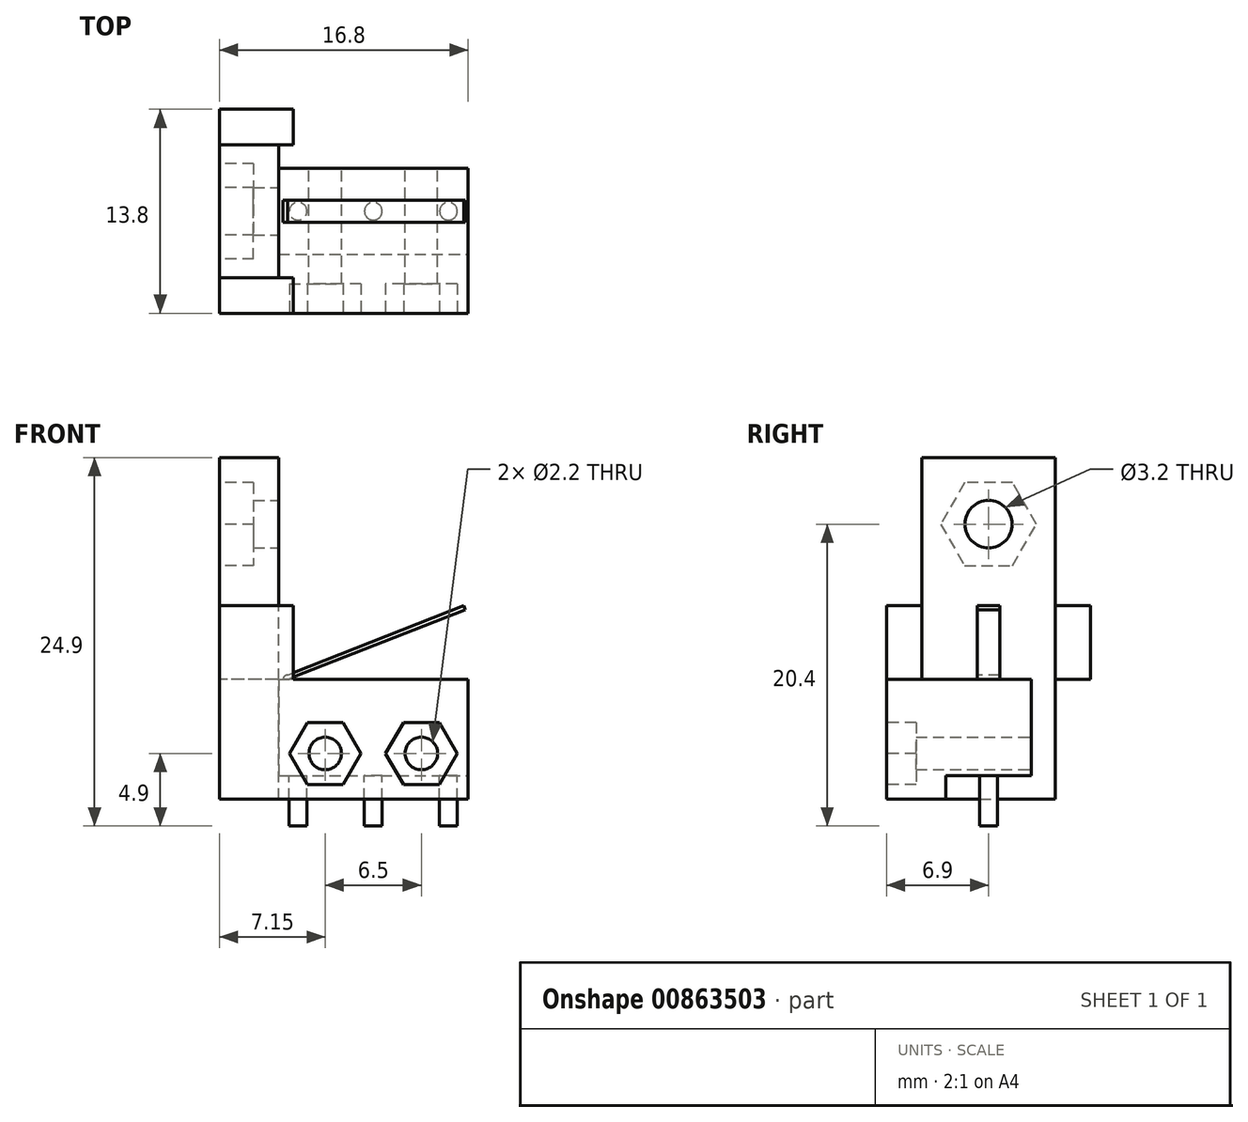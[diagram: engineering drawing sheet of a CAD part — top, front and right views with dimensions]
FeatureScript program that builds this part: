
annotation { "Feature Type Name" : "Feature", "Feature Type Description" : "" }
export const myFeature = defineFeature(function(context is Context, id is Id, definition is map)
    precondition{}
    {
        {
            var Q0;
            Q0=qCreatedBy(makeId("Front.planeOp"),FACE);
            var sketch = newSketch(context, id + "F0", { "sketchPlane" : qUnion([Q0])});
            skLineSegment(sketch, "E0.bottom", {"start": v(-6.4, 6.5) * mm, "end": v(6.4, 6.5) * mm});
            skLineSegment(sketch, "E0.top", {"start": v(-6.4, 0) * mm, "end": v(6.4, 0) * mm});
            skLineSegment(sketch, "E0.left", {"start": v(-6.4, 6.5) * mm, "end": v(-6.4, 0) * mm});
            skLineSegment(sketch, "E0.right", {"start": v(6.4, 6.5) * mm, "end": v(6.4, 0) * mm});
            skCircle(sketch, "E1", {"center": v(3.25, 1.5) * mm, "radius": 1.1 * mm});
            skCircle(sketch, "E2", {"center": v(-3.25, 1.5) * mm, "radius": 1.1 * mm});
            skLineSegment(sketch, "E3", {"start": v(0, 0.48) * mm, "end": v(0, 13.87) * mm, "construction": true});
            skSolve(sketch);
        }
        {
            var Q0;
            Q0=qSketchRegion(id+"F0",true);
            extrude(context, id + "F1", {"entities" : qUnion([Q0]), "depth" : 5.8 * mm});
        }
        {
            var Q0;
            Q0=makeQuery(id+"F1.opExtrude","SWEPT_FACE",FACE,{"disambiguationData":[OSD([sQuery(id+"F0.wireOp",EDGE,"E0.top")])]});
            var sketch = newSketch(context, id + "F2", { "sketchPlane" : qUnion([Q0])});
            skLineSegment(sketch, "E4", {"start": v(0, 12.32) * mm, "end": v(0, -7.08) * mm, "construction": true});
            skCircle(sketch, "E5", {"center": v(-5.08, 2.9) * mm, "radius": 0.6 * mm});
            skCircle(sketch, "E6", {"center": v(0, 2.9) * mm, "radius": 0.6 * mm});
            skCircle(sketch, "E7", {"center": v(5.08, 2.9) * mm, "radius": 0.6 * mm});
            skLineSegment(sketch, "E8", {"start": v(-20.59, 2.9) * mm, "end": v(16.53, 2.9) * mm, "construction": true});
            skPoint(sketch, "E9", {"position": v(-6.4, 2.9) * mm});
            skSolve(sketch);
        }
        {
            var Q0;
            Q0=qSketchRegion(id+"F2",true);
            extrude(context, id + "F3", {"entities" : qUnion([Q0]), "operationType" : NewBodyOperationType.ADD, "depth" : 3.4 * mm});
        }
        {
            var Q0;
            Q0=makeQuery(id+"F1.opExtrude","CAP_FACE",FACE,{"disambiguationData":[OSD([sQuery(id+"F0.wireOp",EDGE,"E0.bottom"),sQuery(id+"F0.wireOp",EDGE,"E0.top"),sQuery(id+"F0.wireOp",EDGE,"E0.left"),sQuery(id+"F0.wireOp",EDGE,"E0.right"),sQuery(id+"F0.wireOp",EDGE,"E1"),sQuery(id+"F0.wireOp",EDGE,"E2")])],"isStart":true});
            var Q1;
            Q1=makeQuery(id+"F1.opExtrude","CAP_FACE",FACE,{"disambiguationData":[OSD([sQuery(id+"F0.wireOp",EDGE,"E0.bottom"),sQuery(id+"F0.wireOp",EDGE,"E0.top"),sQuery(id+"F0.wireOp",EDGE,"E0.left"),sQuery(id+"F0.wireOp",EDGE,"E0.right"),sQuery(id+"F0.wireOp",EDGE,"E1"),sQuery(id+"F0.wireOp",EDGE,"E2")])],"isStart":false});
            cPlane(context, id + "F4", {"entities" : qUnion([Q0, Q1]), "cplaneType" : CPlaneType.MID_PLANE, "offset" : 150 * mm, "width" : 150 * mm, "height" : 150 * mm});
        }
        {
            var Q0;
            Q0=qCreatedBy(id+"F4.planeOp",FACE);
            var sketch = newSketch(context, id + "F5", { "sketchPlane" : qUnion([Q0])});
            skLineSegment(sketch, "E10", {"start": v(16.26, 6.5) * mm, "end": v(-15.15, 6.5) * mm, "construction": true});
            skLineSegment(sketch, "E11", {"start": v(5.8, 6.5) * mm, "end": v(-6.22, 11.22) * mm});
            skLineSegment(sketch, "E12", {"start": v(5.8, 6.8) * mm, "end": v(-6.1, 11.5) * mm});
            skLineSegment(sketch, "E13", {"start": v(-6.1, 11.5) * mm, "end": v(-6.22, 11.22) * mm});
            skLineSegment(sketch, "E14", {"start": v(5.8, 6.5) * mm, "end": v(6.1, 6.5) * mm});
            skArc(sketch, "E15", {"start": v(6.1, 6.5) * mm, "mid": v(6.01, 6.71) * mm, "end": v(5.8, 6.8) * mm});
            skLineSegment(sketch, "E16", {"start": v(5.8, 6.5) * mm, "end": v(5.8, 6.8) * mm, "construction": true});
            skLineSegment(sketch, "E17", {"start": v(15.7, 1.5) * mm, "end": v(-17.73, 1.5) * mm, "construction": true});
            skPoint(sketch, "E18", {"position": v(-3.25, 1.5) * mm});
            skPoint(sketch, "E19", {"position": v(3.25, 1.5) * mm});
            skSolve(sketch);
        }
        {
            var Q0;
            Q0=qSketchRegion(id+"F5",true);
            extrude(context, id + "F6", {"entities" : qUnion([Q0]), "operationType" : NewBodyOperationType.ADD, "depth" : 1.5 * mm, "symmetric" : true});
        }
        {
            var Q0;
            Q0=makeQuery(id+"F1.opExtrude","CAP_FACE",FACE,{"disambiguationData":[OSD([sQuery(id+"F0.wireOp",EDGE,"E0.bottom"),sQuery(id+"F0.wireOp",EDGE,"E0.top"),sQuery(id+"F0.wireOp",EDGE,"E0.left"),sQuery(id+"F0.wireOp",EDGE,"E0.right"),sQuery(id+"F0.wireOp",EDGE,"E1"),sQuery(id+"F0.wireOp",EDGE,"E2")])],"isStart":false});
            var sketch = newSketch(context, id + "F7", { "sketchPlane" : qUnion([Q0])});
            skLineSegment(sketch, "E20.bottom", {"start": v(6.4, -1.6) * mm, "end": v(-6.4, -1.6) * mm});
            skLineSegment(sketch, "E20.top", {"start": v(6.4, 6.5) * mm, "end": v(-6.4, 6.5) * mm});
            skLineSegment(sketch, "E20.left", {"start": v(6.4, -1.6) * mm, "end": v(6.4, 6.5) * mm});
            skLineSegment(sketch, "E20.right", {"start": v(-6.4, -1.6) * mm, "end": v(-6.4, 6.5) * mm});
            skLineSegment(sketch, "E21", {"start": v(0, -13.07) * mm, "end": v(0, 21.12) * mm, "construction": true});
            skPoint(sketch, "E22", {"position": v(3.25, 1.5) * mm});
            skPoint(sketch, "E23", {"position": v(-3.25, 1.5) * mm});
            skLineSegment(sketch, "E24", {"start": v(3.25, 1.5) * mm, "end": v(-3.25, 1.5) * mm, "construction": true});
            skCircle(sketch, "E25", {"center": v(3.25, 1.5) * mm, "radius": 1.1 * mm});
            skCircle(sketch, "E26", {"center": v(-3.25, 1.5) * mm, "radius": 1.1 * mm});
            skSolve(sketch);
        }
        {
            var Q0;
            Q0=qSketchRegion(id+"F7",true);
            extrude(context, id + "F8", {"entities" : qUnion([Q0]), "depth" : 4 * mm});
        }
        {
            var Q0;
            Q0=makeQuery(id+"F8.opExtrude","CAP_FACE",FACE,{"disambiguationData":[OSD([sQuery(id+"F7.wireOp",EDGE,"E20.bottom"),sQuery(id+"F7.wireOp",EDGE,"E20.top"),sQuery(id+"F7.wireOp",EDGE,"E20.left"),sQuery(id+"F7.wireOp",EDGE,"E20.right")])],"isStart":false});
            var sketch = newSketch(context, id + "F9", { "sketchPlane" : qUnion([Q0])});
            skLineSegment(sketch, "E27", {"start": v(-3.25, -7.44) * mm, "end": v(-3.25, 10.28) * mm, "construction": true});
            skCircle(sketch, "E28.cCircle", {"center": v(-3.25, 1.5) * mm, "radius": 2.1 * mm, "construction": true});
            skLineSegment(sketch, "E28.0", {"start": v(-2.04, -0.6) * mm, "end": v(-4.46, -0.6) * mm});
            skLineSegment(sketch, "E28.1", {"start": v(-4.46, -0.6) * mm, "end": v(-5.67, 1.5) * mm});
            skLineSegment(sketch, "E28.2", {"start": v(-5.67, 1.5) * mm, "end": v(-4.46, 3.6) * mm});
            skLineSegment(sketch, "E28.3", {"start": v(-4.46, 3.6) * mm, "end": v(-2.04, 3.6) * mm});
            skLineSegment(sketch, "E28.4", {"start": v(-2.04, 3.6) * mm, "end": v(-0.83, 1.5) * mm});
            skLineSegment(sketch, "E28.5", {"start": v(-0.83, 1.5) * mm, "end": v(-2.04, -0.6) * mm});
            skPoint(sketch, "E28.0.midPoint", {"position": v(-3.25, -0.6) * mm});
            skLineSegment(sketch, "E29", {"start": v(0, -5.2) * mm, "end": v(0, 11) * mm, "construction": true});
            skLineSegment(sketch, "E30.MirrorCS", {"start": v(0.83, 1.5) * mm, "end": v(2.04, -0.6) * mm});
            skPoint(sketch, "E31.MirrorP", {"position": v(3.25, -0.6) * mm});
            skLineSegment(sketch, "E32.MirrorCS", {"start": v(5.67, 1.5) * mm, "end": v(4.46, 3.6) * mm});
            skLineSegment(sketch, "E33.MirrorCS", {"start": v(4.46, 3.6) * mm, "end": v(2.04, 3.6) * mm});
            skLineSegment(sketch, "E34.MirrorCS", {"start": v(2.04, 3.6) * mm, "end": v(0.83, 1.5) * mm});
            skCircle(sketch, "E35.MirrorC", {"center": v(3.25, 1.5) * mm, "radius": 2.1 * mm, "construction": true});
            skLineSegment(sketch, "E36.MirrorCS", {"start": v(4.46, -0.6) * mm, "end": v(5.67, 1.5) * mm});
            skLineSegment(sketch, "E37.MirrorCS", {"start": v(2.04, -0.6) * mm, "end": v(4.46, -0.6) * mm});
            skSolve(sketch);
        }
        {
            var Q0;
            Q0=qSketchRegion(id+"F9",true);
            extrude(context, id + "F10", {"entities" : qUnion([Q0]), "operationType" : NewBodyOperationType.REMOVE, "oppositeDirection" : true, "depth" : 2 * mm});
        }
        {
            var Q0;
            Q0=makeQuery(id+"F1.opExtrude","SWEPT_FACE",FACE,{"disambiguationData":[OSD([sQuery(id+"F0.wireOp",EDGE,"E0.left")])]});
            var sketch = newSketch(context, id + "F11", { "sketchPlane" : qUnion([Q0])});
            skLineSegment(sketch, "E38.top", {"start": v(7.4, 21.5) * mm, "end": v(-1.6, 21.5) * mm});
            skLineSegment(sketch, "E38.left", {"start": v(7.4, 6.5) * mm, "end": v(7.4, 21.5) * mm});
            skLineSegment(sketch, "E38.right", {"start": v(-1.6, -1.6) * mm, "end": v(-1.6, 21.5) * mm});
            skLineSegment(sketch, "E39", {"start": v(2.9, 5.34) * mm, "end": v(2.9, 57.94) * mm, "construction": true});
            skLineSegment(sketch, "E40", {"start": v(7.4, 6.5) * mm, "end": v(9.8, 6.5) * mm});
            skLineSegment(sketch, "E41", {"start": v(9.8, 6.5) * mm, "end": v(9.8, -1.6) * mm});
            skLineSegment(sketch, "E42", {"start": v(9.8, -1.6) * mm, "end": v(-1.6, -1.6) * mm});
            skPoint(sketch, "E43", {"position": v(2.9, 21.5) * mm});
            skLineSegment(sketch, "E44", {"start": v(18.07, 9.5) * mm, "end": v(-14.2, 9.5) * mm, "construction": true});
            skCircle(sketch, "E45", {"center": v(2.9, 17) * mm, "radius": 1.6 * mm});
            skSolve(sketch);
        }
        {
            var Q0;
            Q0=qSketchRegion(id+"F11",true);
            extrude(context, id + "F12", {"entities" : qUnion([Q0]), "operationType" : NewBodyOperationType.ADD, "depth" : 4 * mm});
        }
        {
            var Q0;
            Q0=makeQuery(id+"F12.opExtrude","CAP_FACE",FACE,{"disambiguationData":[OSD([sQuery(id+"F11.wireOp",EDGE,"E38.top"),sQuery(id+"F11.wireOp",EDGE,"E38.left"),sQuery(id+"F11.wireOp",EDGE,"E38.right"),sQuery(id+"F11.wireOp",EDGE,"E40"),sQuery(id+"F11.wireOp",EDGE,"E41"),sQuery(id+"F11.wireOp",EDGE,"E42"),sQuery(id+"F11.wireOp",EDGE,"E45")])],"isStart":false});
            var sketch = newSketch(context, id + "F13", { "sketchPlane" : qUnion([Q0])});
            skLineSegment(sketch, "E46", {"start": v(2.9, 27.74) * mm, "end": v(2.9, 6.94) * mm, "construction": true});
            skPoint(sketch, "E47", {"position": v(2.9, 17) * mm});
            skCircle(sketch, "E48.cCircle", {"center": v(2.9, 17) * mm, "radius": 2.8 * mm, "construction": true});
            skLineSegment(sketch, "E48.0", {"start": v(4.52, 14.2) * mm, "end": v(1.28, 14.2) * mm});
            skLineSegment(sketch, "E48.1", {"start": v(1.28, 14.2) * mm, "end": v(-0.33, 17) * mm});
            skLineSegment(sketch, "E48.2", {"start": v(-0.33, 17) * mm, "end": v(1.28, 19.8) * mm});
            skLineSegment(sketch, "E48.3", {"start": v(1.28, 19.8) * mm, "end": v(4.52, 19.8) * mm});
            skLineSegment(sketch, "E48.4", {"start": v(4.52, 19.8) * mm, "end": v(6.13, 17) * mm});
            skLineSegment(sketch, "E48.5", {"start": v(6.13, 17) * mm, "end": v(4.52, 14.2) * mm});
            skPoint(sketch, "E48.0.midPoint", {"position": v(2.9, 14.2) * mm});
            skSolve(sketch);
        }
        {
            var Q0;
            Q0=qSketchRegion(id+"F13",true);
            extrude(context, id + "F14", {"entities" : qUnion([Q0]), "operationType" : NewBodyOperationType.REMOVE, "oppositeDirection" : true, "depth" : 2.3 * mm});
        }
        {
            var Q0;
            Q0=makeQuery(id+"F12.opExtrude","CAP_FACE",FACE,{"disambiguationData":[OSD([sQuery(id+"F11.wireOp",EDGE,"E38.top"),sQuery(id+"F11.wireOp",EDGE,"E38.left"),sQuery(id+"F11.wireOp",EDGE,"E38.right"),sQuery(id+"F11.wireOp",EDGE,"E40"),sQuery(id+"F11.wireOp",EDGE,"E41"),sQuery(id+"F11.wireOp",EDGE,"E42"),sQuery(id+"F11.wireOp",EDGE,"E45")])],"isStart":false});
            var sketch = newSketch(context, id + "F15", { "sketchPlane" : qUnion([Q0])});
            skLineSegment(sketch, "E49", {"start": v(2.9, -3.9) * mm, "end": v(2.9, 26.18) * mm, "construction": true});
            skLineSegment(sketch, "E50.bottom", {"start": v(9.8, 6.5) * mm, "end": v(7.4, 6.5) * mm});
            skLineSegment(sketch, "E50.top", {"start": v(9.8, 11.5) * mm, "end": v(7.4, 11.5) * mm});
            skLineSegment(sketch, "E50.left", {"start": v(9.8, 6.5) * mm, "end": v(9.8, 11.5) * mm});
            skLineSegment(sketch, "E50.right", {"start": v(7.4, 6.5) * mm, "end": v(7.4, 11.5) * mm});
            skLineSegment(sketch, "E51.MirrorCS", {"start": v(-1.6, 6.5) * mm, "end": v(-1.6, 11.5) * mm});
            skLineSegment(sketch, "E52.MirrorCS", {"start": v(-4, 6.5) * mm, "end": v(-1.6, 6.5) * mm});
            skLineSegment(sketch, "E53.MirrorCS", {"start": v(-4, 11.5) * mm, "end": v(-1.6, 11.5) * mm});
            skLineSegment(sketch, "E54.MirrorCS", {"start": v(-4, 6.5) * mm, "end": v(-4, 11.5) * mm});
            skSolve(sketch);
        }
        {
            var Q0;
            Q0=qSketchRegion(id+"F15",true);
            extrude(context, id + "F16", {"entities" : qUnion([Q0]), "operationType" : NewBodyOperationType.ADD, "oppositeDirection" : true, "depth" : (4 + 1) * mm});
        }
    });
